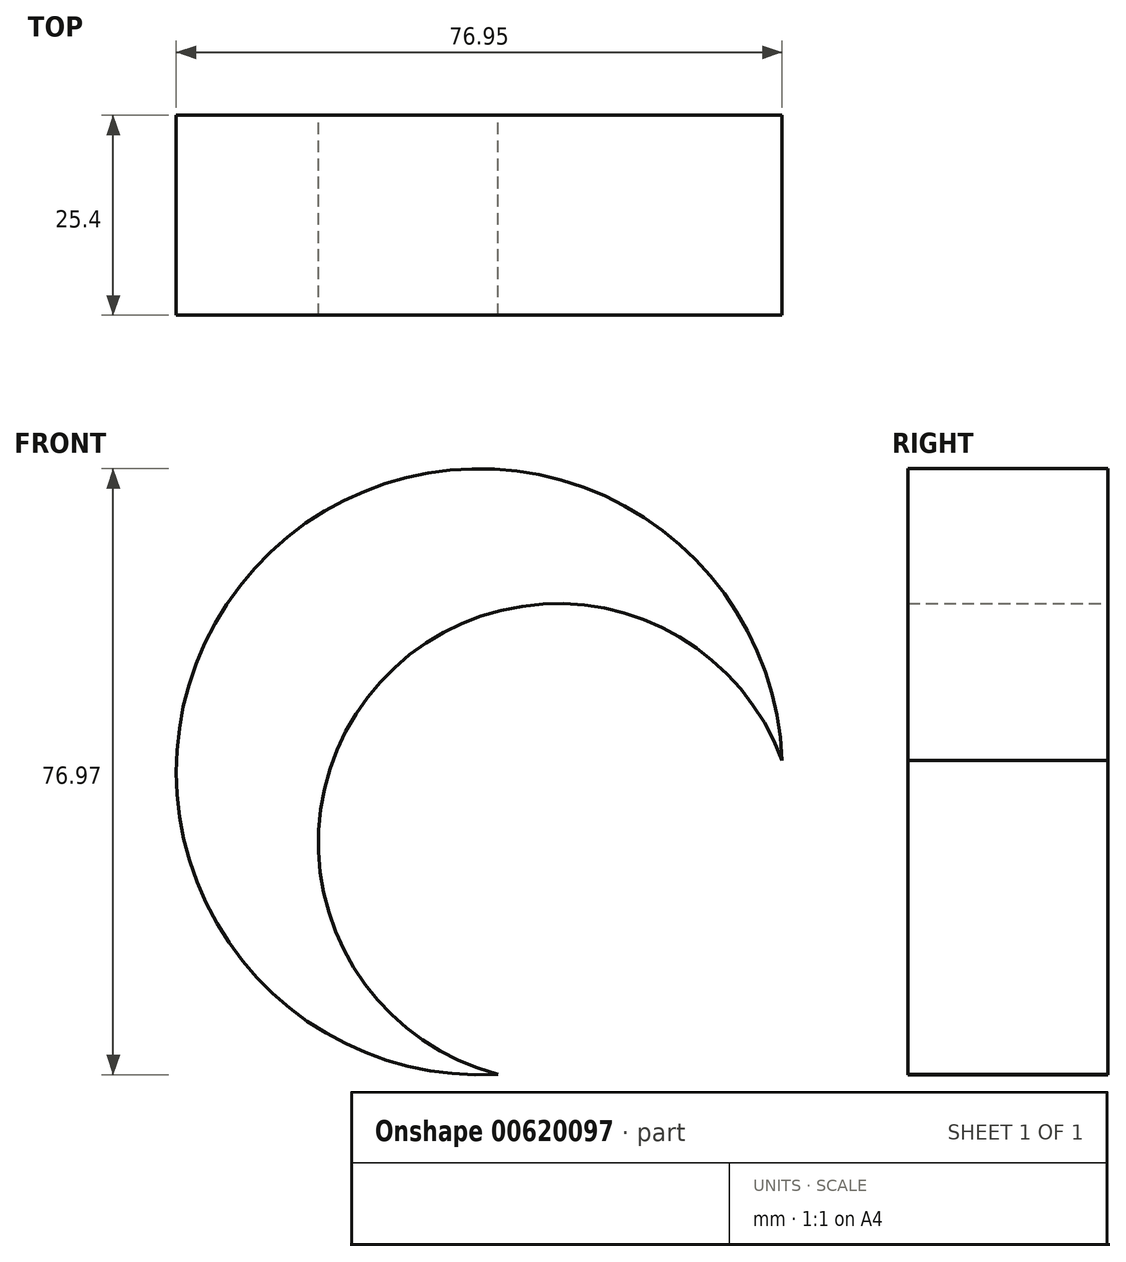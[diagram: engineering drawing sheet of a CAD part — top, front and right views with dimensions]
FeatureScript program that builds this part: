
annotation { "Feature Type Name" : "Feature", "Feature Type Description" : "" }
export const myFeature = defineFeature(function(context is Context, id is Id, definition is map)
    precondition{}
    {
        {
            var Q0;
            Q0=qCreatedBy(makeId("Front.planeOp"),FACE);
            var sketch = newSketch(context, id + "F0", { "sketchPlane" : qUnion([Q0])});
            skArc(sketch, "E0", {"start": v(36.09, 39.83) * mm, "mid": v(-14.93, 49.8) * mm, "end": v(0, 0) * mm});
            skArc(sketch, "E1", {"start": v(36.09, 39.83) * mm, "mid": v(-13.07, 41.48) * mm, "end": v(13.36, 0) * mm});
            skArc(sketch, "E2", {"start": v(36.09, 39.83) * mm, "mid": v(-30.9, 64.26) * mm, "end": v(0, 0) * mm});
            skSolve(sketch);
        }
        {
            var Q0;
            Q0 = qSketchRegion(id + "F0", true);
            extrude(context, id + "F1", {"entities" : qUnion([Q0]), "depth" : 25.4 * mm, "offsetDistance" : 25.4 * mm});
        }
    });
